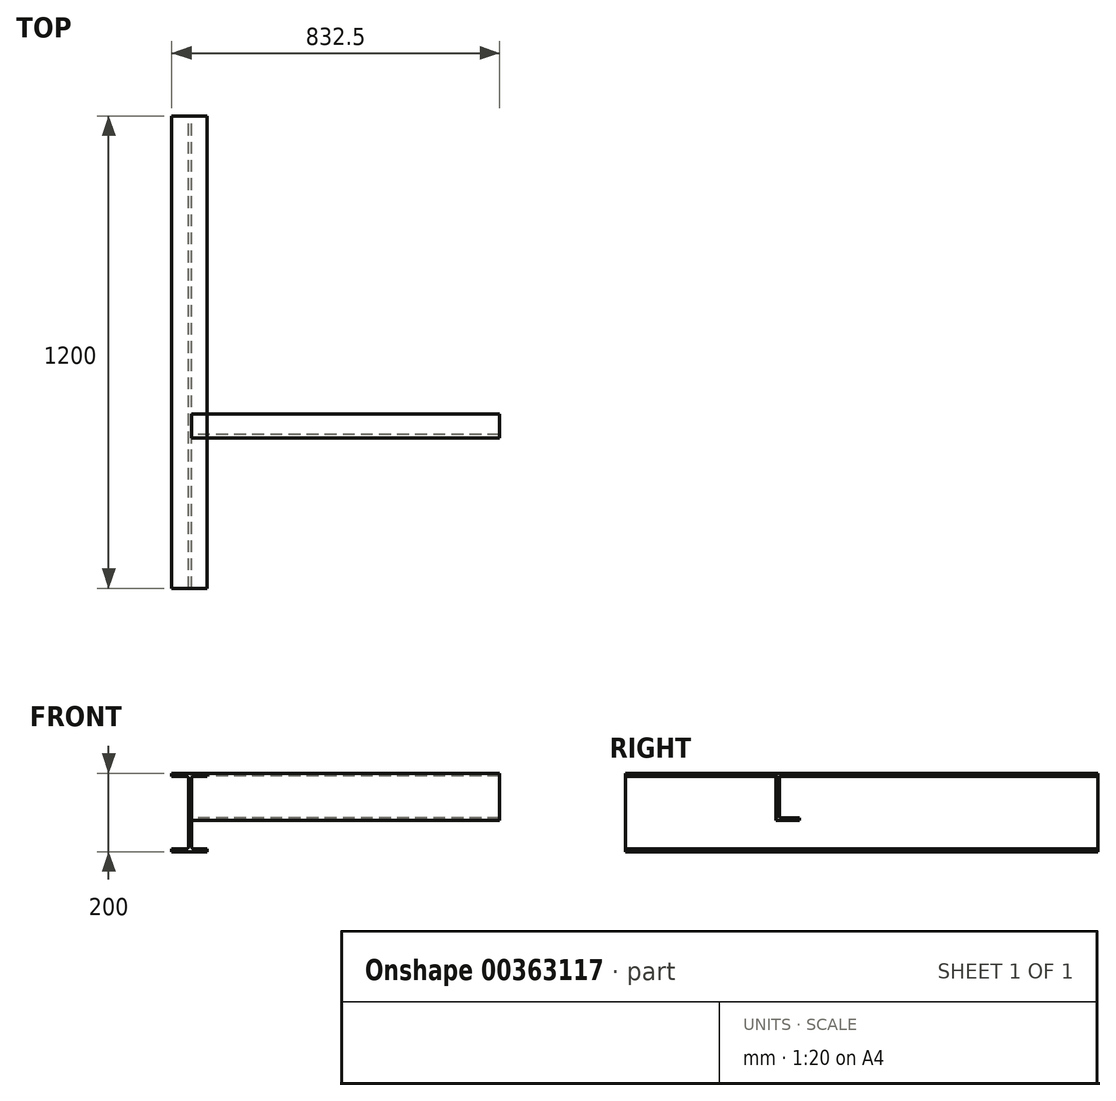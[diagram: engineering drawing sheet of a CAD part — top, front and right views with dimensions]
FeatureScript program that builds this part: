
annotation { "Feature Type Name" : "Feature", "Feature Type Description" : "" }
export const myFeature = defineFeature(function(context is Context, id is Id, definition is map)
    precondition{}
    {
        {
            var Q0;
            Q0=qCreatedBy(makeId("Front.planeOp"),FACE);
            var sketch = newSketch(context, id + "F0", { "sketchPlane" : qUnion([Q0])});
            skLineSegment(sketch, "E0", {"start": v(-45, 97.61) * mm, "end": v(45, 97.61) * mm});
            skPoint(sketch, "E1", {"position": v(0, 97.61) * mm});
            skPoint(sketch, "E1.positionSnap0", {"position": v(0, 97.61) * mm});
            skLineSegment(sketch, "E2", {"start": v(-45, 97.61) * mm, "end": v(-45, 89.61) * mm});
            skLineSegment(sketch, "E3", {"start": v(-45, 89.61) * mm, "end": v(-7.5, 89.61) * mm});
            skLineSegment(sketch, "E4", {"start": v(-2.5, 84.61) * mm, "end": v(-2.5, -89.39) * mm});
            skLineSegment(sketch, "E5", {"start": v(-7.5, -94.39) * mm, "end": v(-45, -94.39) * mm});
            skLineSegment(sketch, "E6", {"start": v(-45, -94.39) * mm, "end": v(-45, -102.39) * mm});
            skLineSegment(sketch, "E7", {"start": v(-45, -102.39) * mm, "end": v(45, -102.39) * mm});
            skLineSegment(sketch, "E8", {"start": v(45, -102.39) * mm, "end": v(45, -94.39) * mm});
            skLineSegment(sketch, "E9", {"start": v(45, -94.39) * mm, "end": v(10.5, -94.39) * mm});
            skLineSegment(sketch, "E10", {"start": v(5.5, -89.39) * mm, "end": v(5.5, 84.61) * mm});
            skLineSegment(sketch, "E11", {"start": v(10.5, 89.61) * mm, "end": v(45, 89.61) * mm});
            skLineSegment(sketch, "E12", {"start": v(45, 89.61) * mm, "end": v(45, 97.61) * mm});
            skPoint(sketch, "E13.visualSharp", {"position": v(-2.5, 89.61) * mm});
            skArc(sketch, "E13.filletArc", {"start": v(-2.5, 84.61) * mm, "mid": v(-3.96, 88.15) * mm, "end": v(-7.5, 89.61) * mm});
            skPoint(sketch, "E14.visualSharp", {"position": v(5.5, 89.61) * mm});
            skArc(sketch, "E14.filletArc", {"start": v(10.5, 89.61) * mm, "mid": v(6.96, 88.15) * mm, "end": v(5.5, 84.61) * mm});
            skPoint(sketch, "E15.visualSharp", {"position": v(-2.5, -94.39) * mm});
            skArc(sketch, "E15.filletArc", {"start": v(-7.5, -94.39) * mm, "mid": v(-3.96, -92.92) * mm, "end": v(-2.5, -89.39) * mm});
            skPoint(sketch, "E16.visualSharp", {"position": v(5.5, -94.39) * mm});
            skArc(sketch, "E16.filletArc", {"start": v(5.5, -89.39) * mm, "mid": v(6.96, -92.92) * mm, "end": v(10.5, -94.39) * mm});
            skSolve(sketch);
        }
        {
            var Q0;
            Q0 = qSketchRegion(id + "F0", true);
            extrude(context, id + "F1", {"entities" : qUnion([Q0]), "depth" : 1200 * mm});
        }
        {
            var Q0;
            Q0=makeQuery(id+"F1.opExtrude","SWEPT_FACE",FACE,{"disambiguationData":[OSD([sQuery(id+"F0.wireOp",EDGE,"E10")])]});
            var sketch = newSketch(context, id + "F2", { "sketchPlane" : qUnion([Q0])});
            skLineSegment(sketch, "E17.0", {"start": v(-1200, 97.61) * mm, "end": v(0, 97.61) * mm});
            skLineSegment(sketch, "E18", {"start": v(-817.8, 97.61) * mm, "end": v(-817.8, -22.39) * mm});
            skLineSegment(sketch, "E19", {"start": v(-817.8, -22.39) * mm, "end": v(-757.8, -22.39) * mm});
            skLineSegment(sketch, "E20", {"start": v(-757.8, -22.39) * mm, "end": v(-757.8, -16.2) * mm});
            skLineSegment(sketch, "E21", {"start": v(-757.8, -16.2) * mm, "end": v(-809.16, -16.2) * mm});
            skLineSegment(sketch, "E22", {"start": v(-809.16, -16.2) * mm, "end": v(-809.16, 91.35) * mm});
            skLineSegment(sketch, "E23", {"start": v(-809.16, 91.35) * mm, "end": v(-757.8, 91.35) * mm});
            skLineSegment(sketch, "E24", {"start": v(-757.8, 91.35) * mm, "end": v(-757.8, 97.61) * mm});
            skLineSegment(sketch, "E25", {"start": v(-817.8, 97.61) * mm, "end": v(-757.8, 97.61) * mm});
            skSolve(sketch);
        }
        {
            var Q0;
            Q0 = qSketchRegion(id + "F2", true);
            extrude(context, id + "F3", {"entities" : qUnion([Q0]), "depth" : 782 * mm});
        }
    });
